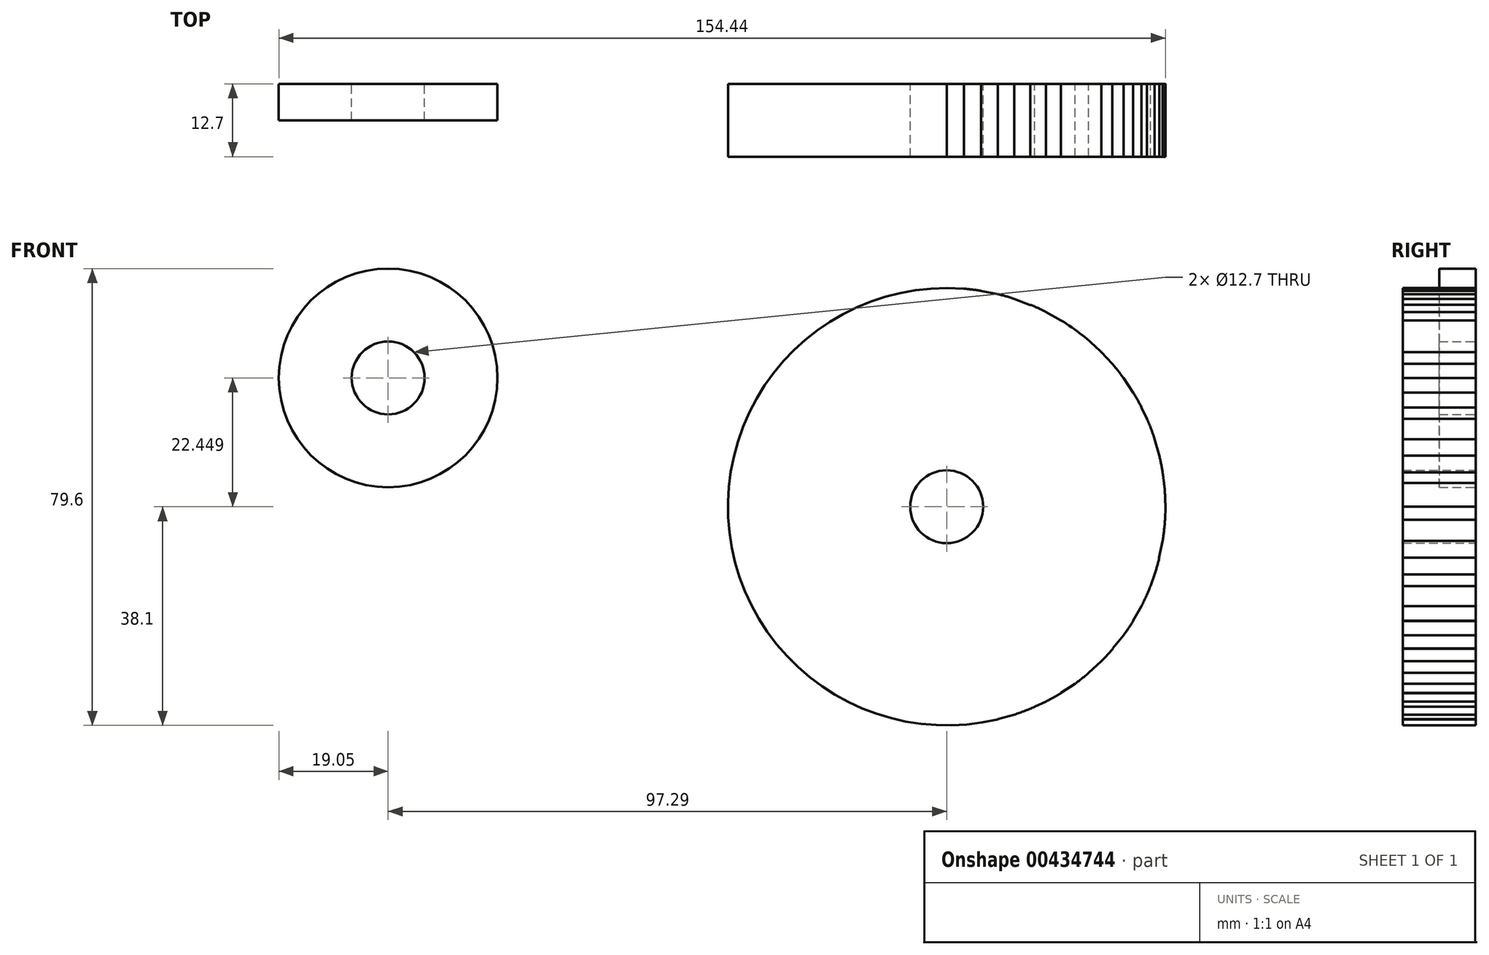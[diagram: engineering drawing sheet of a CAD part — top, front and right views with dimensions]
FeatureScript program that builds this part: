
annotation { "Feature Type Name" : "Feature", "Feature Type Description" : "" }
export const myFeature = defineFeature(function(context is Context, id is Id, definition is map)
    precondition{}
    {
        {
            var Q0;
            Q0=qCreatedBy(makeId("Front.planeOp"),FACE);
            var sketch = newSketch(context, id + "F0", { "sketchPlane" : qUnion([Q0])});
            skCircle(sketch, "E0", {"center": v(0, 0) * mm, "radius": 38.1 * mm});
            skCircle(sketch, "E1", {"center": v(0, 0) * mm, "radius": 6.35 * mm});
            skLineSegment(sketch, "E2", {"start": v(0, 60.2) * mm, "end": v(0, -61.76) * mm, "construction": true});
            skLineSegment(sketch, "E3", {"start": v(-75.2, 0) * mm, "end": v(73.96, 0) * mm, "construction": true});
            skLineSegment(sketch, "E4", {"start": v(-6.2, 78.82) * mm, "end": v(5.14, -65.28) * mm, "construction": true});
            skLineSegment(sketch, "E5", {"start": v(-12.59, 79.48) * mm, "end": v(10.34, -65.3) * mm, "construction": true});
            skLineSegment(sketch, "E6", {"start": v(-21.22, 65.3) * mm, "end": v(21.43, -65.95) * mm, "construction": true});
            skLineSegment(sketch, "E7", {"start": v(-16.38, 68.25) * mm, "end": v(18.75, -78.1) * mm, "construction": true});
            skLineSegment(sketch, "E8", {"start": v(-38.57, 62.94) * mm, "end": v(49.25, -80.37) * mm, "construction": true});
            skLineSegment(sketch, "E9", {"start": v(-47.06, 47.06) * mm, "end": v(71.53, -71.53) * mm, "construction": true});
            skLineSegment(sketch, "E10", {"start": v(-22.15, 53.47) * mm, "end": v(30.4, -73.38) * mm, "construction": true});
            skLineSegment(sketch, "E11", {"start": v(-50.73, 59.4) * mm, "end": v(77.7, -90.97) * mm, "construction": true});
            skLineSegment(sketch, "E12", {"start": v(-28.13, 55.21) * mm, "end": v(27.24, -53.47) * mm, "construction": true});
            skLineSegment(sketch, "E13", {"start": v(-45.73, 62.94) * mm, "end": v(78.46, -107.98) * mm, "construction": true});
            skLineSegment(sketch, "E14", {"start": v(-57.79, 41.99) * mm, "end": v(62, -45.04) * mm, "construction": true});
            skLineSegment(sketch, "E15", {"start": v(-69.2, 22.48) * mm, "end": v(74.5, -24.2) * mm, "construction": true});
            skLineSegment(sketch, "E16", {"start": v(-51.9, 44.32) * mm, "end": v(55.12, -47.08) * mm, "construction": true});
            skLineSegment(sketch, "E17", {"start": v(-62.82, 26.02) * mm, "end": v(73.08, -30.27) * mm, "construction": true});
            skLineSegment(sketch, "E18", {"start": v(-68.78, 35.04) * mm, "end": v(67.46, -34.37) * mm, "construction": true});
            skLineSegment(sketch, "E19", {"start": v(-63.99, 39.21) * mm, "end": v(76.7, -47) * mm, "construction": true});
            skLineSegment(sketch, "E20", {"start": v(-47.5, 11.4) * mm, "end": v(65.28, -15.67) * mm, "construction": true});
            skLineSegment(sketch, "E21", {"start": v(-72.41, 11.47) * mm, "end": v(72.8, -11.53) * mm, "construction": true});
            skLineSegment(sketch, "E22", {"start": v(-69.56, 5.47) * mm, "end": v(74.8, -5.89) * mm, "construction": true});
            skLineSegment(sketch, "E23.MirrorCS", {"start": v(-69.56, -5.47) * mm, "end": v(74.8, 5.89) * mm, "construction": true});
            skLineSegment(sketch, "E24.MirrorCS", {"start": v(-72.41, -11.47) * mm, "end": v(72.8, 11.53) * mm, "construction": true});
            skLineSegment(sketch, "E25.MirrorCS", {"start": v(-47.5, -11.4) * mm, "end": v(65.28, 15.67) * mm, "construction": true});
            skLineSegment(sketch, "E26.MirrorCS", {"start": v(-69.2, -22.48) * mm, "end": v(74.5, 24.2) * mm, "construction": true});
            skLineSegment(sketch, "E27.MirrorCS", {"start": v(-62.82, -26.02) * mm, "end": v(73.08, 30.27) * mm, "construction": true});
            skLineSegment(sketch, "E28.MirrorCS", {"start": v(-68.78, -35.04) * mm, "end": v(67.46, 34.37) * mm, "construction": true});
            skLineSegment(sketch, "E29.MirrorCS", {"start": v(-63.99, -39.21) * mm, "end": v(76.7, 47) * mm, "construction": true});
            skLineSegment(sketch, "E30.MirrorCS", {"start": v(-57.79, -41.99) * mm, "end": v(62, 45.04) * mm, "construction": true});
            skLineSegment(sketch, "E31.MirrorCS", {"start": v(-51.9, -44.32) * mm, "end": v(55.12, 47.08) * mm, "construction": true});
            skLineSegment(sketch, "E32.MirrorCS", {"start": v(-47.06, -47.06) * mm, "end": v(71.53, 71.53) * mm, "construction": true});
            skLineSegment(sketch, "E33.MirrorCS", {"start": v(-50.73, -59.4) * mm, "end": v(77.7, 90.97) * mm, "construction": true});
            skLineSegment(sketch, "E34.MirrorCS", {"start": v(-45.73, -62.94) * mm, "end": v(78.46, 107.98) * mm, "construction": true});
            skLineSegment(sketch, "E35.MirrorCS", {"start": v(-38.57, -62.94) * mm, "end": v(49.25, 80.37) * mm, "construction": true});
            skLineSegment(sketch, "E36.MirrorCS", {"start": v(-28.13, -55.21) * mm, "end": v(27.24, 53.47) * mm, "construction": true});
            skLineSegment(sketch, "E37.MirrorCS", {"start": v(-22.15, -53.47) * mm, "end": v(30.4, 73.38) * mm, "construction": true});
            skLineSegment(sketch, "E38.MirrorCS", {"start": v(-21.22, -65.3) * mm, "end": v(21.43, 65.95) * mm, "construction": true});
            skLineSegment(sketch, "E39.MirrorCS", {"start": v(-16.38, -68.25) * mm, "end": v(18.75, 78.1) * mm, "construction": true});
            skLineSegment(sketch, "E40.MirrorCS", {"start": v(-12.59, -79.48) * mm, "end": v(10.34, 65.3) * mm, "construction": true});
            skLineSegment(sketch, "E41.MirrorCS", {"start": v(-6.2, -78.82) * mm, "end": v(5.14, 65.28) * mm, "construction": true});
            skLineSegment(sketch, "E42", {"start": v(0, 38.1) * mm, "end": v(2.99, 37.98) * mm});
            skLineSegment(sketch, "E43", {"start": v(2.99, 37.98) * mm, "end": v(2.68, 40.69) * mm});
            skLineSegment(sketch, "E44", {"start": v(2.46, 40.9) * mm, "end": v(0.79, 41.04) * mm});
            skLineSegment(sketch, "E45", {"start": v(0.52, 40.77) * mm, "end": v(0, 38.1) * mm});
            skPoint(sketch, "E46.visualSharp", {"position": v(0.5, 41.06) * mm});
            skArc(sketch, "E46.filletArc", {"start": v(0.79, 41.04) * mm, "mid": v(0.6, 40.97) * mm, "end": v(0.52, 40.77) * mm});
            skPoint(sketch, "E47.visualSharp", {"position": v(2.66, 40.9) * mm});
            skArc(sketch, "E47.filletArc", {"start": v(2.68, 40.69) * mm, "mid": v(2.6, 40.84) * mm, "end": v(2.46, 40.9) * mm});
            skLineSegment(sketch, "E48", {"start": v(6, 37.63) * mm, "end": v(8.9, 37.05) * mm});
            skLineSegment(sketch, "E49", {"start": v(8.9, 37.05) * mm, "end": v(9.1, 39.84) * mm});
            skLineSegment(sketch, "E50", {"start": v(8.9, 40.1) * mm, "end": v(7.28, 40.4) * mm});
            skLineSegment(sketch, "E51", {"start": v(7, 40.24) * mm, "end": v(6, 37.63) * mm});
            skArc(sketch, "E52.filletArc", {"start": v(7.28, 40.4) * mm, "mid": v(7.11, 40.37) * mm, "end": v(7, 40.24) * mm});
            skArc(sketch, "E53.filletArc", {"start": v(9.1, 39.84) * mm, "mid": v(9.05, 40.01) * mm, "end": v(8.9, 40.1) * mm});
            skPoint(sketch, "E54", {"position": v(8.9, 37.05) * mm});
            skLineSegment(sketch, "E55", {"start": v(11.77, 36.24) * mm, "end": v(14.56, 35.15) * mm});
            skLineSegment(sketch, "E56", {"start": v(14.56, 35.15) * mm, "end": v(15.17, 37.9) * mm});
            skLineSegment(sketch, "E57", {"start": v(15.01, 38.17) * mm, "end": v(13.48, 38.77) * mm});
            skLineSegment(sketch, "E58", {"start": v(13.17, 38.66) * mm, "end": v(11.77, 36.24) * mm});
            skArc(sketch, "E59.filletArc", {"start": v(13.48, 38.77) * mm, "mid": v(13.3, 38.77) * mm, "end": v(13.17, 38.66) * mm});
            skArc(sketch, "E60.filletArc", {"start": v(15.17, 37.9) * mm, "mid": v(15.14, 38.06) * mm, "end": v(15.01, 38.17) * mm});
            skLineSegment(sketch, "E61", {"start": v(17.3, 33.95) * mm, "end": v(19.93, 32.47) * mm});
            skLineSegment(sketch, "E62", {"start": v(19.9, 32.49) * mm, "end": v(20.92, 35.07) * mm});
            skLineSegment(sketch, "E63", {"start": v(20.81, 35.38) * mm, "end": v(19.38, 36.2) * mm});
            skLineSegment(sketch, "E64", {"start": v(19.04, 36.1) * mm, "end": v(17.3, 33.95) * mm});
            skArc(sketch, "E65.filletArc", {"start": v(19.38, 36.2) * mm, "mid": v(19.2, 36.22) * mm, "end": v(19.04, 36.1) * mm});
            skArc(sketch, "E66.filletArc", {"start": v(20.92, 35.07) * mm, "mid": v(20.92, 35.25) * mm, "end": v(20.81, 35.38) * mm});
            skLineSegment(sketch, "E67", {"start": v(22.4, 30.82) * mm, "end": v(24.74, 28.97) * mm});
            skLineSegment(sketch, "E68", {"start": v(24.74, 28.97) * mm, "end": v(26.12, 31.46) * mm});
            skLineSegment(sketch, "E69", {"start": v(26.05, 31.78) * mm, "end": v(24.74, 32.78) * mm});
            skLineSegment(sketch, "E70", {"start": v(24.45, 32.79) * mm, "end": v(22.4, 30.82) * mm});
            skArc(sketch, "E71.filletArc", {"start": v(24.74, 32.78) * mm, "mid": v(24.6, 32.83) * mm, "end": v(24.45, 32.79) * mm});
            skArc(sketch, "E72.filletArc", {"start": v(26.12, 31.46) * mm, "mid": v(26.14, 31.63) * mm, "end": v(26.05, 31.78) * mm});
            skLineSegment(sketch, "E73", {"start": v(26.94, 26.94) * mm, "end": v(28.98, 24.75) * mm});
            skLineSegment(sketch, "E74", {"start": v(28.98, 24.75) * mm, "end": v(30.72, 26.95) * mm});
            skLineSegment(sketch, "E75", {"start": v(30.7, 27.27) * mm, "end": v(29.58, 28.48) * mm});
            skLineSegment(sketch, "E76", {"start": v(29.26, 28.51) * mm, "end": v(26.94, 26.94) * mm});
            skArc(sketch, "E77.filletArc", {"start": v(29.58, 28.48) * mm, "mid": v(29.43, 28.56) * mm, "end": v(29.26, 28.51) * mm});
            skArc(sketch, "E78.filletArc", {"start": v(30.72, 26.95) * mm, "mid": v(30.77, 27.11) * mm, "end": v(30.7, 27.27) * mm});
            skLineSegment(sketch, "E79", {"start": v(30.82, 22.4) * mm, "end": v(32.45, 19.88) * mm});
            skLineSegment(sketch, "E80", {"start": v(32.45, 19.88) * mm, "end": v(34.54, 21.75) * mm});
            skLineSegment(sketch, "E81", {"start": v(34.59, 22.07) * mm, "end": v(33.69, 23.45) * mm});
            skLineSegment(sketch, "E82", {"start": v(33.38, 23.54) * mm, "end": v(30.82, 22.4) * mm});
            skArc(sketch, "E83.filletArc", {"start": v(33.69, 23.45) * mm, "mid": v(33.55, 23.55) * mm, "end": v(33.38, 23.54) * mm});
            skArc(sketch, "E84.filletArc", {"start": v(34.54, 21.75) * mm, "mid": v(34.62, 21.9) * mm, "end": v(34.59, 22.07) * mm});
            skLineSegment(sketch, "E85", {"start": v(33.95, 17.3) * mm, "end": v(35.23, 14.6) * mm});
            skLineSegment(sketch, "E86", {"start": v(35.23, 14.6) * mm, "end": v(37.55, 16.17) * mm});
            skLineSegment(sketch, "E87", {"start": v(37.63, 16.48) * mm, "end": v(36.93, 17.97) * mm});
            skLineSegment(sketch, "E88", {"start": v(36.63, 18.1) * mm, "end": v(33.95, 17.3) * mm});
            skArc(sketch, "E89.filletArc", {"start": v(36.93, 17.97) * mm, "mid": v(36.8, 18.09) * mm, "end": v(36.63, 18.1) * mm});
            skArc(sketch, "E90.filletArc", {"start": v(37.55, 16.17) * mm, "mid": v(37.65, 16.3) * mm, "end": v(37.63, 16.48) * mm});
            skLineSegment(sketch, "E91", {"start": v(36.24, 11.77) * mm, "end": v(37.03, 8.89) * mm});
            skLineSegment(sketch, "E92", {"start": v(37.03, 8.89) * mm, "end": v(39.59, 10.03) * mm});
            skLineSegment(sketch, "E93", {"start": v(39.72, 10.33) * mm, "end": v(39.29, 11.92) * mm});
            skLineSegment(sketch, "E94", {"start": v(39.02, 12.1) * mm, "end": v(36.24, 11.77) * mm});
            skArc(sketch, "E95.filletArc", {"start": v(39.29, 11.92) * mm, "mid": v(39.19, 12.06) * mm, "end": v(39.02, 12.1) * mm});
            skArc(sketch, "E96.filletArc", {"start": v(39.59, 10.03) * mm, "mid": v(39.7, 10.15) * mm, "end": v(39.72, 10.33) * mm});
            skLineSegment(sketch, "E97", {"start": v(37.63, 5.96) * mm, "end": v(38.03, 3) * mm});
            skLineSegment(sketch, "E98", {"start": v(38.03, 3) * mm, "end": v(40.72, 3.78) * mm});
            skLineSegment(sketch, "E99", {"start": v(40.9, 4.05) * mm, "end": v(40.67, 5.7) * mm});
            skLineSegment(sketch, "E100", {"start": v(40.43, 5.9) * mm, "end": v(37.63, 5.96) * mm});
            skArc(sketch, "E101.filletArc", {"start": v(40.67, 5.7) * mm, "mid": v(40.6, 5.84) * mm, "end": v(40.43, 5.9) * mm});
            skArc(sketch, "E102.filletArc", {"start": v(40.72, 3.78) * mm, "mid": v(40.85, 3.89) * mm, "end": v(40.9, 4.05) * mm});
            skLineSegment(sketch, "E103", {"start": v(38.1, 0) * mm, "end": v(38.01, -3) * mm});
            skLineSegment(sketch, "E104", {"start": v(38.01, -3) * mm, "end": v(40.8, -2.65) * mm});
            skLineSegment(sketch, "E105", {"start": v(41, -2.4) * mm, "end": v(41.06, -0.76) * mm});
            skLineSegment(sketch, "E106", {"start": v(40.86, -0.5) * mm, "end": v(38.1, 0) * mm});
            skArc(sketch, "E107.filletArc", {"start": v(41.06, -0.76) * mm, "mid": v(41, -0.6) * mm, "end": v(40.86, -0.5) * mm});
            skArc(sketch, "E108.filletArc", {"start": v(40.8, -2.65) * mm, "mid": v(40.95, -2.57) * mm, "end": v(41, -2.4) * mm});
            skLineSegment(sketch, "E109.MirrorCS", {"start": v(75.2, 0) * mm, "end": v(-73.96, 0) * mm, "construction": true});
            skLineSegment(sketch, "E110", {"start": v(37.63, -5.96) * mm, "end": v(37, -8.88) * mm});
            skLineSegment(sketch, "E111", {"start": v(37, -8.88) * mm, "end": v(39.8, -9.05) * mm});
            skLineSegment(sketch, "E112", {"start": v(40.05, -8.86) * mm, "end": v(40.4, -7.25) * mm});
            skLineSegment(sketch, "E113", {"start": v(40.25, -6.96) * mm, "end": v(37.63, -5.96) * mm});
            skArc(sketch, "E114.filletArc", {"start": v(40.4, -7.25) * mm, "mid": v(40.38, -7.08) * mm, "end": v(40.25, -6.96) * mm});
            skArc(sketch, "E115.filletArc", {"start": v(39.8, -9.05) * mm, "mid": v(39.96, -9) * mm, "end": v(40.05, -8.86) * mm});
            skLineSegment(sketch, "E116", {"start": v(36.24, -11.77) * mm, "end": v(35.23, -14.6) * mm});
            skLineSegment(sketch, "E117", {"start": v(35.23, -14.6) * mm, "end": v(37.98, -15.12) * mm});
            skLineSegment(sketch, "E118", {"start": v(38.26, -14.96) * mm, "end": v(38.82, -13.4) * mm});
            skLineSegment(sketch, "E119", {"start": v(38.7, -13.1) * mm, "end": v(36.24, -11.77) * mm});
            skArc(sketch, "E120.filletArc", {"start": v(38.82, -13.4) * mm, "mid": v(38.81, -13.23) * mm, "end": v(38.7, -13.1) * mm});
            skArc(sketch, "E121.filletArc", {"start": v(37.98, -15.12) * mm, "mid": v(38.15, -15.1) * mm, "end": v(38.26, -14.96) * mm});
            skLineSegment(sketch, "E122", {"start": v(33.95, -17.3) * mm, "end": v(32.47, -19.9) * mm});
            skLineSegment(sketch, "E123", {"start": v(32.47, -19.9) * mm, "end": v(35.09, -20.9) * mm});
            skLineSegment(sketch, "E124", {"start": v(35.4, -20.79) * mm, "end": v(36.2, -19.35) * mm});
            skLineSegment(sketch, "E125", {"start": v(36.14, -19.04) * mm, "end": v(33.95, -17.3) * mm});
            skArc(sketch, "E126.filletArc", {"start": v(36.2, -19.35) * mm, "mid": v(36.23, -19.18) * mm, "end": v(36.14, -19.04) * mm});
            skArc(sketch, "E127.filletArc", {"start": v(35.09, -20.9) * mm, "mid": v(35.26, -20.9) * mm, "end": v(35.4, -20.79) * mm});
            skLineSegment(sketch, "E128", {"start": v(30.82, -22.4) * mm, "end": v(28.92, -24.7) * mm});
            skLineSegment(sketch, "E129", {"start": v(28.92, -24.7) * mm, "end": v(31.32, -26.14) * mm});
            skLineSegment(sketch, "E130", {"start": v(31.64, -26.08) * mm, "end": v(32.7, -24.81) * mm});
            skLineSegment(sketch, "E131", {"start": v(32.69, -24.5) * mm, "end": v(30.82, -22.4) * mm});
            skArc(sketch, "E132.filletArc", {"start": v(32.7, -24.81) * mm, "mid": v(32.75, -24.65) * mm, "end": v(32.69, -24.5) * mm});
            skArc(sketch, "E133.filletArc", {"start": v(31.32, -26.14) * mm, "mid": v(31.49, -26.17) * mm, "end": v(31.64, -26.08) * mm});
            skLineSegment(sketch, "E134", {"start": v(26.94, -26.94) * mm, "end": v(24.72, -28.94) * mm});
            skLineSegment(sketch, "E135", {"start": v(24.72, -28.94) * mm, "end": v(26.89, -30.72) * mm});
            skLineSegment(sketch, "E136", {"start": v(27.2, -30.7) * mm, "end": v(28.43, -29.6) * mm});
            skLineSegment(sketch, "E137", {"start": v(28.48, -29.29) * mm, "end": v(26.94, -26.94) * mm});
            skArc(sketch, "E138.filletArc", {"start": v(28.43, -29.6) * mm, "mid": v(28.51, -29.45) * mm, "end": v(28.48, -29.29) * mm});
            skArc(sketch, "E139.filletArc", {"start": v(26.89, -30.72) * mm, "mid": v(27.05, -30.77) * mm, "end": v(27.2, -30.7) * mm});
            skLineSegment(sketch, "E140", {"start": v(22.4, -30.82) * mm, "end": v(19.89, -32.45) * mm});
            skLineSegment(sketch, "E141", {"start": v(19.89, -32.45) * mm, "end": v(21.75, -34.54) * mm});
            skLineSegment(sketch, "E142", {"start": v(22.07, -34.59) * mm, "end": v(23.46, -33.69) * mm});
            skLineSegment(sketch, "E143", {"start": v(23.55, -33.38) * mm, "end": v(22.4, -30.82) * mm});
            skArc(sketch, "E144.filletArc", {"start": v(23.46, -33.69) * mm, "mid": v(23.56, -33.55) * mm, "end": v(23.55, -33.38) * mm});
            skArc(sketch, "E145.filletArc", {"start": v(21.75, -34.54) * mm, "mid": v(21.9, -34.62) * mm, "end": v(22.07, -34.59) * mm});
            skLineSegment(sketch, "E146", {"start": v(17.3, -33.95) * mm, "end": v(14.6, -35.23) * mm});
            skLineSegment(sketch, "E147", {"start": v(14.6, -35.23) * mm, "end": v(16.17, -37.55) * mm});
            skLineSegment(sketch, "E148", {"start": v(16.48, -37.63) * mm, "end": v(17.97, -36.93) * mm});
            skLineSegment(sketch, "E149", {"start": v(18.1, -36.63) * mm, "end": v(17.3, -33.95) * mm});
            skArc(sketch, "E150.filletArc", {"start": v(17.97, -36.93) * mm, "mid": v(18.09, -36.8) * mm, "end": v(18.1, -36.63) * mm});
            skArc(sketch, "E151.filletArc", {"start": v(16.17, -37.55) * mm, "mid": v(16.3, -37.65) * mm, "end": v(16.48, -37.63) * mm});
            skLineSegment(sketch, "E152", {"start": v(11.77, -36.24) * mm, "end": v(8.89, -37.03) * mm});
            skLineSegment(sketch, "E153", {"start": v(8.89, -37.03) * mm, "end": v(10.03, -39.59) * mm});
            skLineSegment(sketch, "E154", {"start": v(10.33, -39.72) * mm, "end": v(11.92, -39.29) * mm});
            skLineSegment(sketch, "E155", {"start": v(12.1, -39.02) * mm, "end": v(11.77, -36.24) * mm});
            skArc(sketch, "E156.filletArc", {"start": v(11.92, -39.29) * mm, "mid": v(12.06, -39.19) * mm, "end": v(12.1, -39.02) * mm});
            skArc(sketch, "E157.filletArc", {"start": v(10.03, -39.59) * mm, "mid": v(10.15, -39.7) * mm, "end": v(10.33, -39.72) * mm});
            skLineSegment(sketch, "E158", {"start": v(5.96, -37.63) * mm, "end": v(3.02, -38.17) * mm});
            skLineSegment(sketch, "E159", {"start": v(3.02, -38.17) * mm, "end": v(3.94, -40.82) * mm});
            skLineSegment(sketch, "E160", {"start": v(4.21, -40.98) * mm, "end": v(5.84, -40.68) * mm});
            skLineSegment(sketch, "E161", {"start": v(6.04, -40.43) * mm, "end": v(5.96, -37.63) * mm});
            skArc(sketch, "E162.filletArc", {"start": v(5.84, -40.68) * mm, "mid": v(5.98, -40.6) * mm, "end": v(6.04, -40.43) * mm});
            skArc(sketch, "E163.filletArc", {"start": v(3.94, -40.82) * mm, "mid": v(4.04, -40.95) * mm, "end": v(4.21, -40.98) * mm});
            skSolve(sketch);
        }
        {
            var Q0;
            Q0=makeQuery(id+"F0.imprint","IMPRINT",FACE,{"disambiguationData":[TD([[makeQuery(id+"F0.imprint","IMPRINT",EDGE,{"derivedFrom":sQuery(id+"F0.wireOp",EDGE,"E0")}),1.0]])]});
            var Q1;
            Q1 = qSketchRegion(id + "F2", true);
            extrude(context, id + "F1", {"entities" : qUnion([Q0, Q1]), "depth" : 12.7 * mm});
        }
        {
            var Q0;
            Q0=qCreatedBy(makeId("Front.planeOp"),FACE);
            var sketch = newSketch(context, id + "F2", { "sketchPlane" : qUnion([Q0])});
            skCircle(sketch, "E164", {"center": v(-97.3, 22.45) * mm, "radius": 19.05 * mm});
            skCircle(sketch, "E165", {"center": v(-97.3, 22.45) * mm, "radius": 6.35 * mm});
            skSolve(sketch);
        }
        {
            var Q0;
            Q0 = qSketchRegion(id + "F2", true);
            extrude(context, id + "F3", {"entities" : qUnion([Q0]), "operationType" : NewBodyOperationType.ADD, "depth" : 6.35 * mm});
        }
    });
